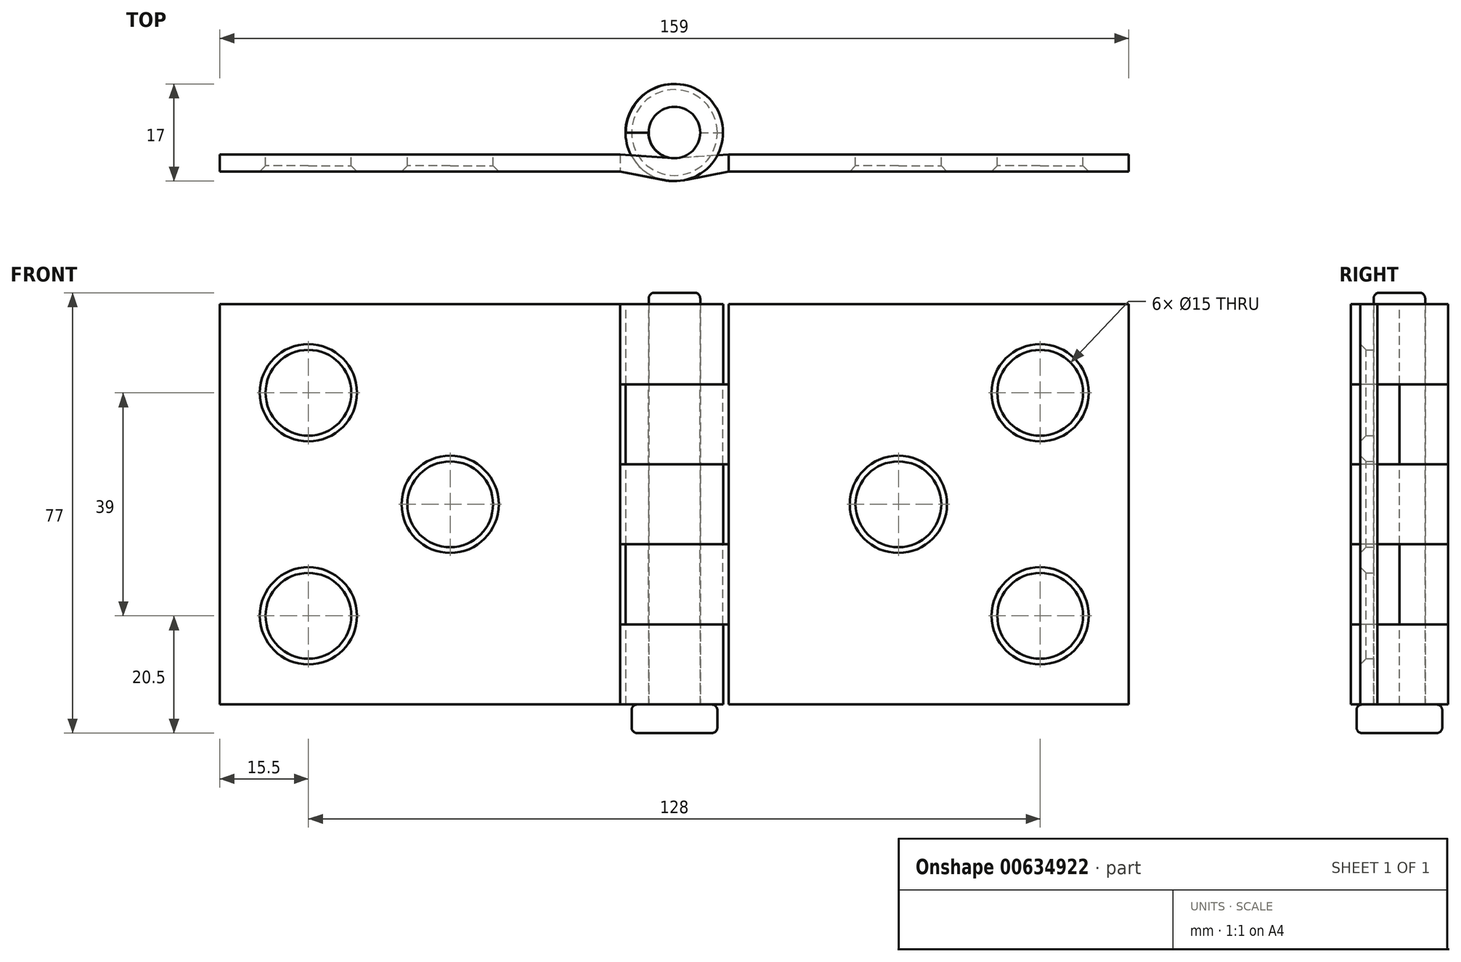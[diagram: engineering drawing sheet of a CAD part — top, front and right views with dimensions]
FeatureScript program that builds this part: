
annotation { "Feature Type Name" : "Feature", "Feature Type Description" : "" }
export const myFeature = defineFeature(function(context is Context, id is Id, definition is map)
    precondition{}
    {
        {
            var Q0;
            Q0=qCreatedBy(makeId("Top.planeOp"),FACE);
            var sketch = newSketch(context, id + "F0", { "sketchPlane" : qUnion([Q0])});
            skLineSegment(sketch, "E0.bottom", {"start": v(-70, 0) * mm, "end": v(0, 0) * mm});
            skLineSegment(sketch, "E0.top", {"start": v(-70, 3) * mm, "end": v(0, 3) * mm});
            skLineSegment(sketch, "E0.left", {"start": v(-70, 0) * mm, "end": v(-70, 3) * mm});
            skArc(sketch, "E1", {"start": v(7.93, -1.52) * mm, "mid": v(16.08, 12.25) * mm, "end": v(1.03, 6.83) * mm});
            skArc(sketch, "E2", {"start": v(9.21, 2.34) * mm, "mid": v(12.82, 9.9) * mm, "end": v(5.03, 6.83) * mm});
            skLineSegment(sketch, "E3", {"start": v(5.03, 6.83) * mm, "end": v(1.03, 6.83) * mm});
            skLineSegment(sketch, "E4", {"start": v(0, 3) * mm, "end": v(9.21, 2.34) * mm});
            skLineSegment(sketch, "E5", {"start": v(0, 0) * mm, "end": v(7.93, -1.52) * mm});
            skSolve(sketch);
        }
        {
            var Q0;
            Q0 = qSketchRegion(id + "F0", true);
            extrude(context, id + "F1", {"entities" : qUnion([Q0]), "oppositeDirection" : true, "depth" : 70 * mm, "offsetDistance" : 25 * mm});
        }
        {
            var Q0;
            Q0=makeQuery(id+"F1.opExtrude","SWEPT_FACE",FACE,{"disambiguationData":[OSD([sQuery(id+"F0.wireOp",EDGE,"E0.top")])]});
            var sketch = newSketch(context, id + "F2", { "sketchPlane" : qUnion([Q0])});
            skCircle(sketch, "E6", {"center": v(54.5, -54.5) * mm, "radius": 7.5 * mm});
            skCircle(sketch, "E7", {"center": v(29.7, -35) * mm, "radius": 7.5 * mm});
            skCircle(sketch, "E8", {"center": v(54.5, -15.5) * mm, "radius": 7.5 * mm});
            skSolve(sketch);
        }
        {
            var Q0;
            Q0=makeQuery(id+"F2.imprint","IMPRINT",FACE,{"disambiguationData":[TD([[makeQuery(id+"F2.imprint","IMPRINT",EDGE,{"derivedFrom":sQuery(id+"F2.wireOp",EDGE,"E7")}),1.0]])]});
            var Q1;
            Q1=makeQuery(id+"F2.imprint","IMPRINT",FACE,{"disambiguationData":[TD([[makeQuery(id+"F2.imprint","IMPRINT",EDGE,{"derivedFrom":sQuery(id+"F2.wireOp",EDGE,"E8")}),1.0]])]});
            var Q2;
            Q2=makeQuery(id+"F2.imprint","IMPRINT",FACE,{"disambiguationData":[TD([[makeQuery(id+"F2.imprint","IMPRINT",EDGE,{"derivedFrom":sQuery(id+"F2.wireOp",EDGE,"E6")}),1.0]])]});
            extrude(context, id + "F3", {"entities" : qUnion([Q0, Q1, Q2]), "operationType" : NewBodyOperationType.REMOVE, "oppositeDirection" : true, "depth" : 25 * mm, "offsetDistance" : 25 * mm});
        }
        {
            var Q0;
            Q0=makeQuery(id+"F3.boolean.opBoolean","INTERSECT",EDGE,{"derivedFrom":[makeQuery(id+"F1.opExtrude","SWEPT_FACE",FACE,{"disambiguationData":[OSD([sQuery(id+"F0.wireOp",EDGE,"E0.bottom")])]}),makeQuery(id+"F3.opExtrude","SWEPT_FACE",FACE,{"disambiguationData":[OSD([sQuery(id+"F2.wireOp",EDGE,"E8")])]})]});
            var Q1;
            Q1=makeQuery(id+"F3.boolean.opBoolean","COPY",EDGE,{"derivedFrom":makeQuery(id+"F3.opExtrude","CAP_EDGE",EDGE,{"disambiguationData":[OSD([sQuery(id+"F2.wireOp",EDGE,"E7")])],"isStart":true})});
            var Q2;
            Q2=makeQuery(id+"F3.boolean.opBoolean","INTERSECT",EDGE,{"derivedFrom":[makeQuery(id+"F1.opExtrude","SWEPT_FACE",FACE,{"disambiguationData":[OSD([sQuery(id+"F0.wireOp",EDGE,"E0.bottom")])]}),makeQuery(id+"F3.opExtrude","SWEPT_FACE",FACE,{"disambiguationData":[OSD([sQuery(id+"F2.wireOp",EDGE,"E7")])]})]});
            var Q3;
            Q3=makeQuery(id+"F3.boolean.opBoolean","INTERSECT",EDGE,{"derivedFrom":[makeQuery(id+"F1.opExtrude","SWEPT_FACE",FACE,{"disambiguationData":[OSD([sQuery(id+"F0.wireOp",EDGE,"E0.bottom")])]}),makeQuery(id+"F3.opExtrude","SWEPT_FACE",FACE,{"disambiguationData":[OSD([sQuery(id+"F2.wireOp",EDGE,"E6")])]})]});
            var Q4;
            Q4=makeQuery(id+"F3.boolean.opBoolean","COPY",EDGE,{"derivedFrom":makeQuery(id+"F3.opExtrude","CAP_EDGE",EDGE,{"disambiguationData":[OSD([sQuery(id+"F2.wireOp",EDGE,"E6")])],"isStart":true})});
            var Q5;
            Q5=makeQuery(id+"F3.boolean.opBoolean","COPY",EDGE,{"derivedFrom":makeQuery(id+"F3.opExtrude","CAP_EDGE",EDGE,{"disambiguationData":[OSD([sQuery(id+"F2.wireOp",EDGE,"E8")])],"isStart":true})});
            chamfer(context, id + "F4", {"entities" : qUnion([Q0, Q1, Q2, Q3, Q4, Q5]), "width" : 1 * mm, "tangentPropagation" : true});
        }
        {
            var Q0;
            Q0=qCreatedBy(makeId("Right.planeOp"),FACE);
            cPlane(context, id + "F5", {"entities" : qUnion([Q0]), "cplaneType" : CPlaneType.OFFSET, "offset" : 40 * mm, "width" : 150 * mm, "height" : 150 * mm});
        }
        {
            var Q0;
            Q0=makeQuery(id+"F1.opExtrude","SWEPT_BODY",BODY,{"disambiguationData":[OSD([sQuery(id+"F0.wireOp",EDGE,"E0.bottom"),sQuery(id+"F0.wireOp",EDGE,"E0.top"),sQuery(id+"F0.wireOp",EDGE,"E0.left"),sQuery(id+"F0.wireOp",EDGE,"E1"),sQuery(id+"F0.wireOp",EDGE,"E2"),sQuery(id+"F0.wireOp",EDGE,"E3"),sQuery(id+"F0.wireOp",EDGE,"E4"),sQuery(id+"F0.wireOp",EDGE,"E5")])]});
            var Q1;
            Q1=qCreatedBy(id+"F5.planeOp",FACE);
            mirror(context, id + "F6", {"entities" : qUnion([Q0]), "mirrorPlane" : qUnion([Q1])});
        }
        {
            var Q0;
            Q0=makeQuery(id+"F6.opPattern","COPY",FACE,{"derivedFrom":makeQuery(id+"F1.opExtrude","SWEPT_FACE",FACE,{"disambiguationData":[OSD([sQuery(id+"F0.wireOp",EDGE,"E0.top")])]}),"instanceName":"1"});
            var sketch = newSketch(context, id + "F7", { "sketchPlane" : qUnion([Q0])});
            skLineSegment(sketch, "E9.bottom", {"start": v(-80, 0) * mm, "end": v(-47, 0) * mm});
            skLineSegment(sketch, "E9.top", {"start": v(-80, -14) * mm, "end": v(-47, -14) * mm});
            skLineSegment(sketch, "E9.left", {"start": v(-80, 0) * mm, "end": v(-80, -14) * mm});
            skLineSegment(sketch, "E9.right", {"start": v(-47, 0) * mm, "end": v(-47, -14) * mm});
            skLineSegment(sketch, "E10.bottom", {"start": v(-80, -28) * mm, "end": v(-47, -28) * mm});
            skLineSegment(sketch, "E10.top", {"start": v(-80, -42) * mm, "end": v(-47, -42) * mm});
            skLineSegment(sketch, "E10.left", {"start": v(-80, -28) * mm, "end": v(-80, -42) * mm});
            skLineSegment(sketch, "E10.right", {"start": v(-47, -28) * mm, "end": v(-47, -42) * mm});
            skLineSegment(sketch, "E11.bottom", {"start": v(-80, -70) * mm, "end": v(-47, -70) * mm});
            skLineSegment(sketch, "E11.top", {"start": v(-80, -56) * mm, "end": v(-47, -56) * mm});
            skLineSegment(sketch, "E11.left", {"start": v(-80, -70) * mm, "end": v(-80, -56) * mm});
            skLineSegment(sketch, "E11.right", {"start": v(-47, -70) * mm, "end": v(-47, -56) * mm});
            skLineSegment(sketch, "E12.bottom", {"start": v(0, -14) * mm, "end": v(-33, -14) * mm});
            skLineSegment(sketch, "E12.top", {"start": v(0, -28) * mm, "end": v(-33, -28) * mm});
            skLineSegment(sketch, "E12.left", {"start": v(0, -14) * mm, "end": v(0, -28) * mm});
            skLineSegment(sketch, "E12.right", {"start": v(-33, -14) * mm, "end": v(-33, -28) * mm});
            skLineSegment(sketch, "E13.bottom", {"start": v(0, -42) * mm, "end": v(-30.33, -42) * mm});
            skLineSegment(sketch, "E13.top", {"start": v(0, -56) * mm, "end": v(-30.33, -56) * mm});
            skLineSegment(sketch, "E13.left", {"start": v(0, -42) * mm, "end": v(0, -56) * mm});
            skLineSegment(sketch, "E13.right", {"start": v(-30.33, -42) * mm, "end": v(-30.33, -56) * mm});
            skSolve(sketch);
        }
        {
            var Q0;
            Q0=makeQuery(id+"F7.imprint","IMPRINT",FACE,{"disambiguationData":[TD([[makeQuery(id+"F7.imprint","IMPRINT",EDGE,{"derivedFrom":sQuery(id+"F7.wireOp",EDGE,"E12.bottom")}),1.0]])]});
            var Q1;
            Q1=makeQuery(id+"F7.imprint","IMPRINT",FACE,{"disambiguationData":[TD([[makeQuery(id+"F7.imprint","IMPRINT",EDGE,{"derivedFrom":sQuery(id+"F7.wireOp",EDGE,"E9.bottom")}),-1.0]])]});
            var Q2;
            Q2=makeQuery(id+"F7.imprint","IMPRINT",FACE,{"disambiguationData":[TD([[makeQuery(id+"F7.imprint","IMPRINT",EDGE,{"derivedFrom":sQuery(id+"F7.wireOp",EDGE,"E10.bottom")}),-1.0]])]});
            var Q3;
            Q3=makeQuery(id+"F7.imprint","IMPRINT",FACE,{"disambiguationData":[TD([[makeQuery(id+"F7.imprint","IMPRINT",EDGE,{"derivedFrom":sQuery(id+"F7.wireOp",EDGE,"E13.bottom")}),1.0]])]});
            var Q4;
            Q4=makeQuery(id+"F7.imprint","IMPRINT",FACE,{"disambiguationData":[TD([[makeQuery(id+"F7.imprint","IMPRINT",EDGE,{"derivedFrom":sQuery(id+"F7.wireOp",EDGE,"E11.bottom")}),1.0]])]});
            extrude(context, id + "F8", {"entities" : qUnion([Q0, Q1, Q2, Q3, Q4]), "operationType" : NewBodyOperationType.REMOVE, "depth" : 30 * mm, "offsetDistance" : 25 * mm, "symmetric" : true});
        }
        {
            var Q0;
            Q0=makeQuery(id+"F1.opExtrude","SWEPT_BODY",BODY,{"disambiguationData":[OSD([sQuery(id+"F0.wireOp",EDGE,"E0.bottom"),sQuery(id+"F0.wireOp",EDGE,"E0.top"),sQuery(id+"F0.wireOp",EDGE,"E0.left"),sQuery(id+"F0.wireOp",EDGE,"E1"),sQuery(id+"F0.wireOp",EDGE,"E2"),sQuery(id+"F0.wireOp",EDGE,"E3"),sQuery(id+"F0.wireOp",EDGE,"E4"),sQuery(id+"F0.wireOp",EDGE,"E5")])]});
            transform(context, id + "F9", {"entities" : qUnion([Q0]), "transformType" : TransformType.TRANSLATION_3D, "dx" : 61 * mm, "dy" : 0 * mm, "dz" : 0 * mm, "makeCopy" : false});
        }
        {
            var Q0;
            Q0=makeQuery(id+"F1.opExtrude","CAP_FACE",FACE,{"disambiguationData":[OSD([sQuery(id+"F0.wireOp",EDGE,"E0.bottom"),sQuery(id+"F0.wireOp",EDGE,"E0.top"),sQuery(id+"F0.wireOp",EDGE,"E0.left"),sQuery(id+"F0.wireOp",EDGE,"E1"),sQuery(id+"F0.wireOp",EDGE,"E2"),sQuery(id+"F0.wireOp",EDGE,"E3"),sQuery(id+"F0.wireOp",EDGE,"E4"),sQuery(id+"F0.wireOp",EDGE,"E5")])],"isStart":false});
            var sketch = newSketch(context, id + "F10", { "sketchPlane" : qUnion([Q0])});
            skCircle(sketch, "E14", {"center": v(70.53, -6.83) * mm, "radius": 4.5 * mm});
            skSolve(sketch);
        }
        {
            var Q0;
            Q0 = qSketchRegion(id + "F10", true);
            extrude(context, id + "F11", {"entities" : qUnion([Q0]), "oppositeDirection" : true, "depth" : 72 * mm, "offsetDistance" : 25 * mm});
        }
        {
            var Q0;
            Q0=makeQuery(id+"F11.opExtrude","CAP_FACE",FACE,{"disambiguationData":[OSD([sQuery(id+"F10.wireOp",EDGE,"E14")])],"isStart":true});
            var sketch = newSketch(context, id + "F12", { "sketchPlane" : qUnion([Q0])});
            skCircle(sketch, "E15", {"center": v(70.53, -6.83) * mm, "radius": 7.5 * mm});
            skSolve(sketch);
        }
        {
            var Q0;
            Q0 = qSketchRegion(id + "F12", true);
            extrude(context, id + "F13", {"entities" : qUnion([Q0]), "depth" : 5 * mm, "offsetDistance" : 25 * mm});
        }
        {
            var Q0;
            Q0=makeQuery(id+"F13.opExtrude","CAP_EDGE",EDGE,{"disambiguationData":[OSD([sQuery(id+"F12.wireOp",EDGE,"E15")])],"isStart":false});
            var Q1;
            Q1=makeQuery(id+"F13.opExtrude","SWEPT_FACE",FACE,{"disambiguationData":[OSD([sQuery(id+"F12.wireOp",EDGE,"E15")])]});
            fillet(context, id + "F14", {"entities" : qUnion([Q0, Q1]), "radius" : 1 * mm, "tangentPropagation" : true, "allowEdgeOverflow" : false});
        }
        {
            var Q0;
            Q0=makeQuery(id+"F11.opExtrude","CAP_EDGE",EDGE,{"disambiguationData":[OSD([sQuery(id+"F10.wireOp",EDGE,"E14")])],"isStart":false});
            fillet(context, id + "F15", {"entities" : qUnion([Q0]), "radius" : 1 * mm, "tangentPropagation" : true, "allowEdgeOverflow" : false});
        }
    });
